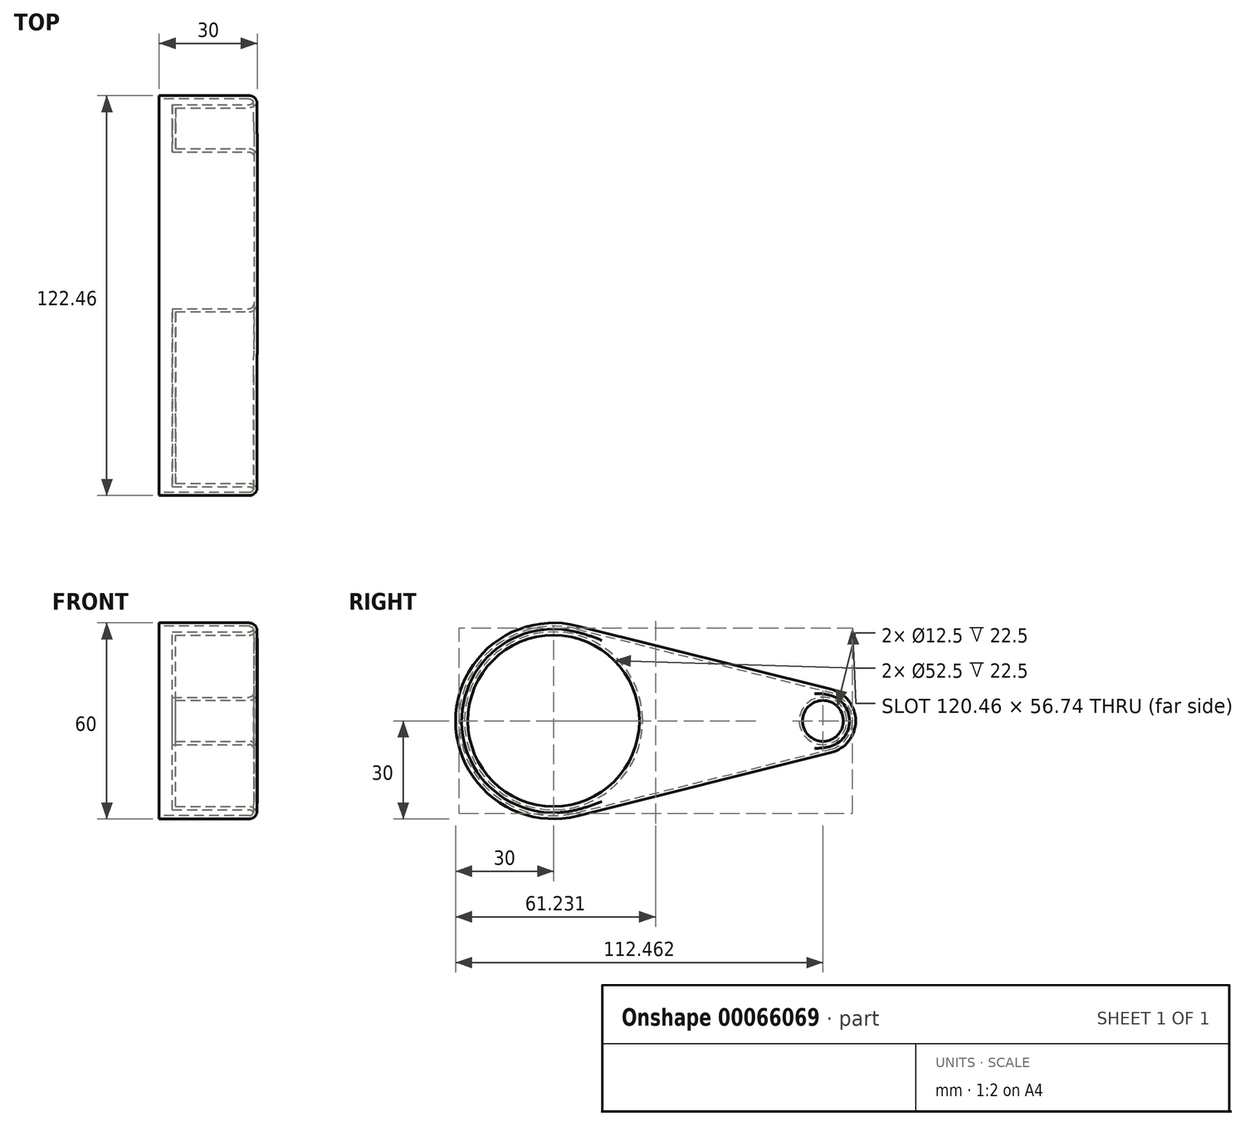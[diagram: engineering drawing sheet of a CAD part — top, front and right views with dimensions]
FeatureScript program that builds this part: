
annotation { "Feature Type Name" : "Feature", "Feature Type Description" : "" }
export const myFeature = defineFeature(function(context is Context, id is Id, definition is map)
    precondition{}
    {
        {
            var Q0;
            Q0=qCreatedBy(makeId("Right.planeOp"),FACE);
            var sketch = newSketch(context, id + "F0", { "sketchPlane" : qUnion([Q0])});
            skCircle(sketch, "E0", {"center": v(0, 0) * mm, "radius": 30 * mm});
            skCircle(sketch, "E1", {"center": v(82.46, 0) * mm, "radius": 10 * mm});
            skLineSegment(sketch, "E2", {"start": v(7.28, 29.1) * mm, "end": v(84.89, 9.7) * mm});
            skLineSegment(sketch, "E3", {"start": v(7.28, -29.1) * mm, "end": v(84.89, -9.7) * mm});
            skSolve(sketch);
        }
        {
            var Q0;
            {var subQ0=sQuery(id+"F0.wireOp",EDGE,"E2");Q0=makeQuery(id+"F0.imprint","IMPRINT",FACE,{"disambiguationData":[TD([[makeQuery(id+"F0.imprint","IMPRINT",EDGE,{"derivedFrom":subQ0}),-1.0]])]});}
            var Q1;
            {var subQ0=sQuery(id+"F0.wireOp",EDGE,"E0");var subQ1=makeQuery(id+"F0.imprint","INTERSECT",VERTEX,{"derivedFrom":[subQ0,sQuery(id+"F0.wireOp",EDGE,"E2")]});Q1=makeQuery(id+"F0.imprint","IMPRINT",FACE,{"disambiguationData":[TD([[makeQuery(id+"F0.imprint","IMPRINT",EDGE,{"disambiguationData":[TD([[subQ1,-1.0]])],"derivedFrom":subQ0}),1.0]])]});}
            var Q2;
            {var subQ0=sQuery(id+"F0.wireOp",EDGE,"E1");var subQ1=makeQuery(id+"F0.imprint","INTERSECT",VERTEX,{"derivedFrom":[subQ0,sQuery(id+"F0.wireOp",EDGE,"E2")]});Q2=makeQuery(id+"F0.imprint","IMPRINT",FACE,{"disambiguationData":[TD([[makeQuery(id+"F0.imprint","IMPRINT",EDGE,{"disambiguationData":[TD([[subQ1,-1.0]])],"derivedFrom":subQ0}),1.0]])]});}
            extrude(context, id + "F1", {"entities" : qUnion([Q0, Q1, Q2]), "depth" : 30 * mm});
        }
        {
            var Q0;
            Q0=makeQuery(id+"F1.opExtrude","CAP_FACE",FACE,{"disambiguationData":[OSD([sQuery(id+"F0.wireOp",EDGE,"E0"),sQuery(id+"F0.wireOp",EDGE,"E1"),sQuery(id+"F0.wireOp",EDGE,"E2"),sQuery(id+"F0.wireOp",EDGE,"E3")])],"isStart":false});
            var sketch = newSketch(context, id + "F2", { "sketchPlane" : qUnion([Q0])});
            skCircle(sketch, "E4", {"center": v(0, 0) * mm, "radius": 26.25 * mm});
            skCircle(sketch, "E5", {"center": v(82.46, 0) * mm, "radius": 6.25 * mm});
            skSolve(sketch);
        }
        {
            var Q0;
            Q0 = qSketchRegion(id + "F2", true);
            extrude(context, id + "F3", {"entities" : qUnion([Q0]), "operationType" : NewBodyOperationType.REMOVE, "oppositeDirection" : true, "depth" : 25 * mm});
        }
        {
            var Q0;
            Q0=makeQuery(id+"F1.opExtrude","CAP_FACE",FACE,{"disambiguationData":[OSD([sQuery(id+"F0.wireOp",EDGE,"E0"),sQuery(id+"F0.wireOp",EDGE,"E1"),sQuery(id+"F0.wireOp",EDGE,"E2"),sQuery(id+"F0.wireOp",EDGE,"E3")])],"isStart":false});
            fillet(context, id + "F4", {"entities" : qUnion([Q0]), "radius" : 2.5 * mm, "tangentPropagation" : true, "allowEdgeOverflow" : false});
        }
        {
            var Q0;
            Q0=makeQuery(id+"F1.opExtrude","CAP_FACE",FACE,{"disambiguationData":[OSD([sQuery(id+"F0.wireOp",EDGE,"E0"),sQuery(id+"F0.wireOp",EDGE,"E1"),sQuery(id+"F0.wireOp",EDGE,"E2"),sQuery(id+"F0.wireOp",EDGE,"E3")])],"isStart":true});
            shell(context, id + "F5", {"entities" : qUnion([Q0]), "thickness" : 1 * mm});
        }
    });
